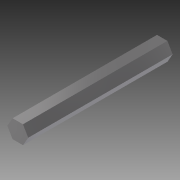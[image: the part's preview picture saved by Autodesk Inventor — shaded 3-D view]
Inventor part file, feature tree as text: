
AUTODESK INVENTOR PART (.ipt)
format: ipt  version: 2014 (Build 180170000, 170)  size: 75,776 bytes
history: native  units: in
note: dims shown in document units (in); Inventor stores cm internally (conversion verified against a paired STEP export)
features: extrude x1, sketch x1
ambient origin geometry x8: Origin, YZ Plane, XZ Plane, XY Plane, X Axis, Y Axis, Z Axis, Center Point
bodies: Solid1 (feature_tree)
feature tree (2):
  extrude  "Extrusion1"  Depth=3.0in TaperAngle=0.0deg
  sketch  "Sketch1"  dims[d0=0.375in d1=3.0in d2=0.0in]
